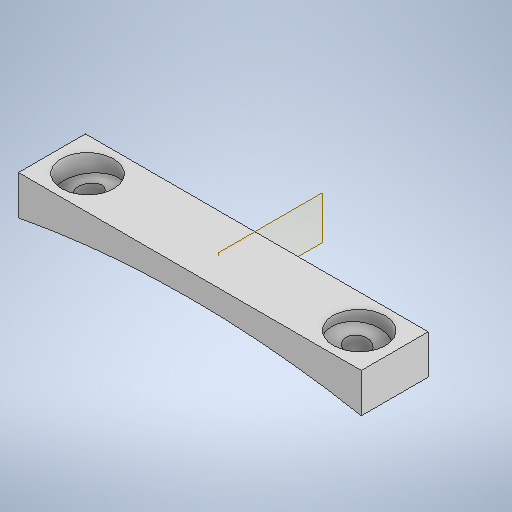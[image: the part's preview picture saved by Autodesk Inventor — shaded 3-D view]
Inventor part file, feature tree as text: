
AUTODESK INVENTOR PART (.ipt)
format: ipt  version: 2025 (Build 290162000, 162)  size: 332,800 bytes
history: native  units: in
note: dims shown in document units (in); Inventor stores cm internally (conversion verified against a paired STEP export)
features: sketch x5, extrude x4, mirror x2, revolve x1, plane x1
ambient origin geometry x8: Origin, YZ Plane, XZ Plane, XY Plane, X Axis, Y Axis, Z Axis, Center Point
bodies: Solid1 (feature_tree)
feature tree (13):
  extrude  "Extrusion1"  Depth=1.5in
  revolve  "Revolution1"  [1 undecoded]
  extrude  "Extrusion2"  Depth=0.0563in
  plane  "Work Plane9"
  mirror  "Mirror1"
  extrude  "Extrusion3"  TaperAngle=90.0deg  [1 undecoded]
  mirror  "Mirror2"
  extrude  "Extrusion4"  TaperAngle=90.0deg  [1 undecoded]
  sketch  "Sketch1"  dims[d2=0.25in d3=1.5in]
  sketch  "Sketch2"  dims[d4=1.0in d5=0.0in d6=0.1in]
  sketch  "Sketch3"  dims[d7=0.12in d8=0.0563in]
  sketch  "Sketch5"  dims[d9=0.2in d10=90.0deg]
  sketch  "Sketch6"  dims[d11=0.275in d12=90.0deg d13=0.15in d14=0.6748in d15=0.1in d16=180.0deg d17=1.0in d18=0.0in d27=-1.8228in d28=1.0in d29=0.0in d30=0.356in d31=90.0deg d32=0.712in d33=1.0in d34=0.0in]
note: 3 required parameter values undecoded (feature->parameter linkage not recoverable at this tier; creation-order binding heuristic only, values carry confidence <= 0.55)